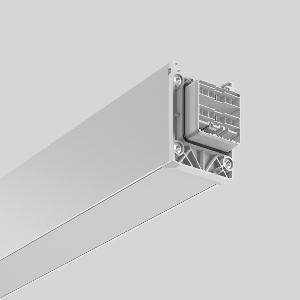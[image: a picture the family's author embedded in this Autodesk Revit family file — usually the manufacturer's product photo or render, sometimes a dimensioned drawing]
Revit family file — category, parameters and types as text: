
# Revit family: linedo_4_5m_00_00000000_954500_000_500_900_b482
name_source: partatom
category: Lighting Fixtures
units: mm (PartAtom-declared; Revit-internal decimal feet)

## family parameters
Cut with Voids When Loaded = No
Host = Face
Light Source = No
Part Type = Normal
Room Calculation Point = No
Round Connector Dimension = Use Diameter
Shared = No

## types (1)
- LINEDO_4,5m_00_00000000
    Apparent Load = 0 VA
    Default Elevation = 1800 mm
    Description = Series: LINEDO
Rapid-installation complete module for universal use as a continuous line luminaire. Blank module. System profile made of aluminium extrusion profile, anodised. Cover made of plastic, surface like housing. Simple, tool-free installation of system profiles using separate accessories for cable, chain or ceiling suspension. Tool-free connection and mechanical connectors to secure. Please order supply module, connection and mounting accessories separately. Luminaire with limited surface temperature in accordance with EN  60598-2-24 for use in environments in which a deposit of non-conductive dust on the luminaire can be expected. 
Colour: anodised aluminium
Length: 4566 mm
Width: 58 mm
Height: 76 mm
Weight: 7,92 kg
Type of Installation: Ceiling mounting, Suspension cable/chain
    Height = 76 mm
    Lamp = 0 x
    Length = 4547 mm
    Luminous efficacy = 0 lm/W
    Manufacturer = RZB
    ModVariant = No
    Model = 954500.000.500.900
    Mounting Place = Ceiling
    Mounting Type = Surface mounted, Pendant
    Number of Poles = 1
    OnlyDefault = Yes
    Power Factor = 1
    Product Name = LINEDO_4,5m_00_00000000
    Product group = Continuous line luminaire system Linedo IP 54
    ProductGroupID = 314
    Protection Class = Protection class I
    Protection Degree = IP 54
    RLX_Detail_Level = 1
    RLX_Emergency_Light_Flux = 0 lm
    RLX_Emergency_Type = 0
    RLX_Emergency_Type_DB = No
    RlxData = <blob elided: 31361 chars, md5=4f6acc82>
    Standby Power = 0 W
    System Light Flux = 0 lm
    System Power = 0 W
    Type Comments = Product without accessories
    Type Image = 954500.000.400.900.jpg
    URL = http://relux.com
    VarID = ---
    Voltage = 230 V
    Voltage Range = 220-240 V
    Weight = 0.00 kg
    Width = 58 mm

## geometry (parser evidence)
native form markers: Blend x4, Sweep x10
no freeform markers — native parametric forms only
